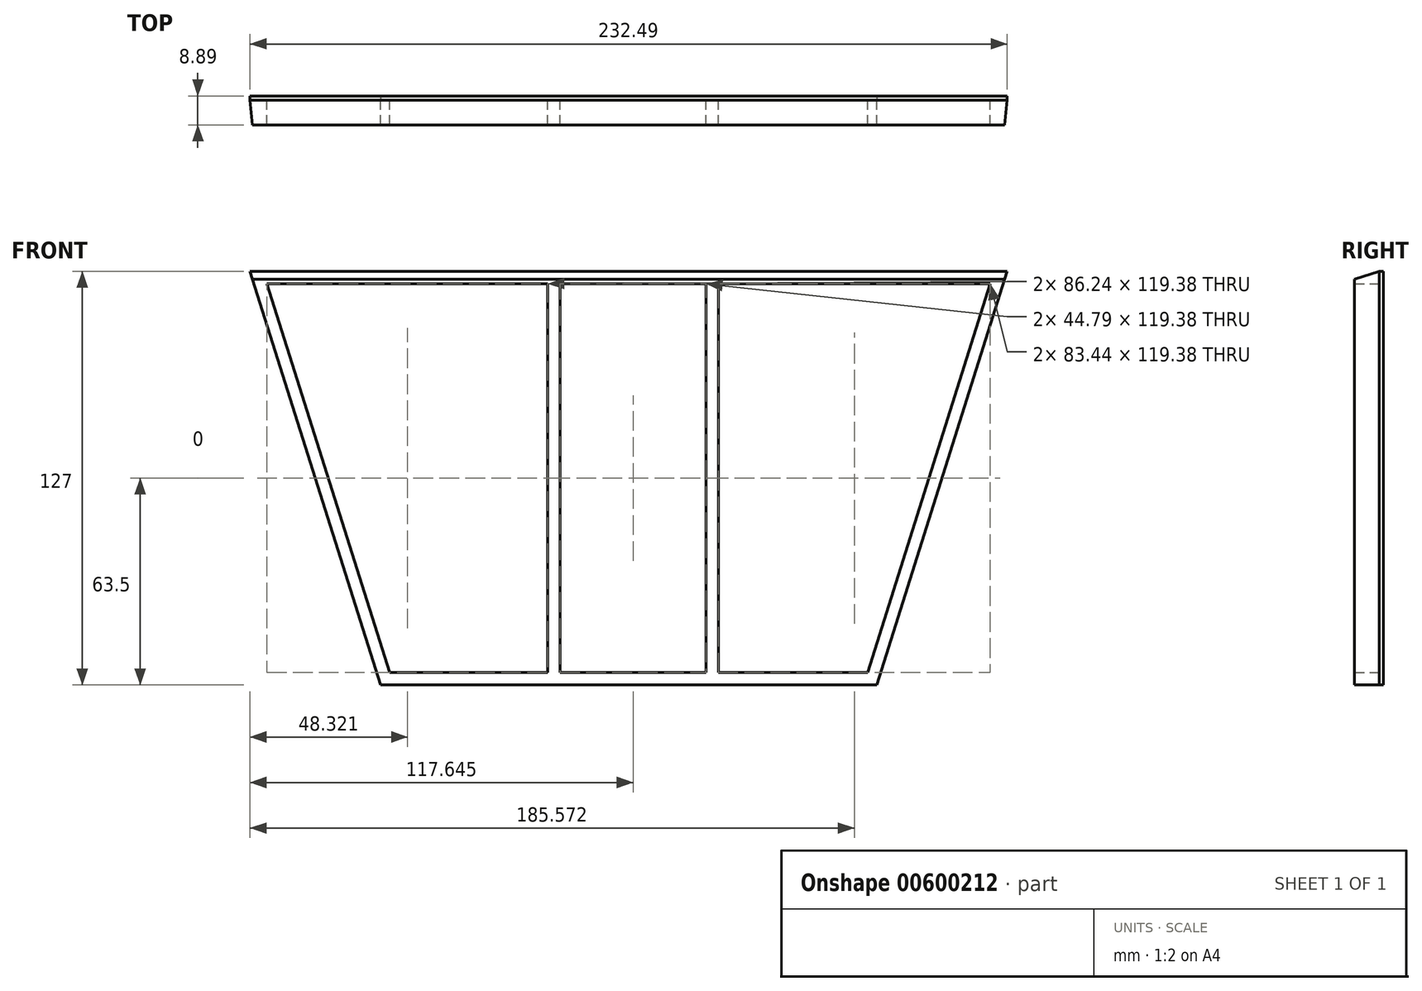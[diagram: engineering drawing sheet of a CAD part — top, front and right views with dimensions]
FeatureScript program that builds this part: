
annotation { "Feature Type Name" : "Feature", "Feature Type Description" : "" }
export const myFeature = defineFeature(function(context is Context, id is Id, definition is map)
    precondition{}
    {
        {
            var Q0;
            Q0=qCreatedBy(makeId("Front.planeOp"),FACE);
            var sketch = newSketch(context, id + "F0", { "sketchPlane" : qUnion([Q0])});
            skLineSegment(sketch, "E0", {"start": v(0, 0) * mm, "end": v(-232.49, 0) * mm});
            skLineSegment(sketch, "E1", {"start": v(-232.49, 0) * mm, "end": v(-192.44, -127) * mm});
            skLineSegment(sketch, "E2", {"start": v(-192.44, -127) * mm, "end": v(-40.04, -127) * mm});
            skLineSegment(sketch, "E3", {"start": v(-40.04, -127) * mm, "end": v(0, 0) * mm});
            skLineSegment(sketch, "E4.0", {"start": v(-5.2, -3.8) * mm, "end": v(-227.29, -3.81) * mm});
            skLineSegment(sketch, "E4.1", {"start": v(-42.84, -123.2) * mm, "end": v(-5.2, -3.81) * mm});
            skLineSegment(sketch, "E4.2", {"start": v(-189.65, -123.2) * mm, "end": v(-42.84, -123.2) * mm});
            skLineSegment(sketch, "E4.3", {"start": v(-227.29, -3.81) * mm, "end": v(-189.65, -123.2) * mm});
            skLineSegment(sketch, "E5", {"start": v(-141.05, -3.81) * mm, "end": v(-141.05, -123.2) * mm});
            skLineSegment(sketch, "E6", {"start": v(-137.24, -3.81) * mm, "end": v(-137.24, -123.2) * mm});
            skLineSegment(sketch, "E7", {"start": v(-92.45, -3.81) * mm, "end": v(-92.45, -123.2) * mm});
            skLineSegment(sketch, "E8", {"start": v(-88.64, -3.81) * mm, "end": v(-88.64, -123.2) * mm});
            skLineSegment(sketch, "E9.bottom", {"start": v(-189.65, -123.2) * mm, "end": v(-185.84, -123.2) * mm});
            skLineSegment(sketch, "E9.top", {"start": v(-189.65, -3.81) * mm, "end": v(-185.84, -3.81) * mm});
            skLineSegment(sketch, "E9.left", {"start": v(-189.65, -123.2) * mm, "end": v(-189.65, -3.81) * mm});
            skLineSegment(sketch, "E9.right", {"start": v(-185.84, -123.2) * mm, "end": v(-185.84, -3.81) * mm});
            skLineSegment(sketch, "E10.bottom", {"start": v(-42.84, -123.2) * mm, "end": v(-46.65, -123.2) * mm});
            skLineSegment(sketch, "E10.top", {"start": v(-42.84, -3.8) * mm, "end": v(-46.65, -3.8) * mm});
            skLineSegment(sketch, "E10.left", {"start": v(-42.84, -123.2) * mm, "end": v(-42.84, -3.8) * mm});
            skLineSegment(sketch, "E10.right", {"start": v(-46.65, -123.2) * mm, "end": v(-46.65, -3.8) * mm});
            skSolve(sketch);
        }
        {
            var Q0;
            Q0=makeQuery(id+"F0.imprint","IMPRINT",FACE,{"disambiguationData":[TD([[makeQuery(id+"F0.imprint","IMPRINT",EDGE,{"derivedFrom":sQuery(id+"F0.wireOp",EDGE,"E0")}),1.0]])]});
            var Q1;
            {var subQ0=sQuery(id+"F0.wireOp",EDGE,"E5");Q1=makeQuery(id+"F0.imprint","IMPRINT",FACE,{"disambiguationData":[TD([[makeQuery(id+"F0.imprint","IMPRINT",EDGE,{"derivedFrom":subQ0}),1.0]])]});}
            var Q2;
            {var subQ0=sQuery(id+"F0.wireOp",EDGE,"E7");Q2=makeQuery(id+"F0.imprint","IMPRINT",FACE,{"disambiguationData":[TD([[makeQuery(id+"F0.imprint","IMPRINT",EDGE,{"derivedFrom":subQ0}),1.0]])]});}
            var Q3;
            Q3=makeQuery(id+"F0.imprint","IMPRINT",FACE,{"disambiguationData":[TD([[makeQuery(id+"F0.imprint","IMPRINT",EDGE,{"derivedFrom":sQuery(id+"F0.wireOp",EDGE,"E9.bottom")}),1.0]])]});
            var Q4;
            Q4=makeQuery(id+"F0.imprint","IMPRINT",FACE,{"disambiguationData":[TD([[makeQuery(id+"F0.imprint","IMPRINT",EDGE,{"derivedFrom":sQuery(id+"F0.wireOp",EDGE,"E10.bottom")}),-1.0]])]});
            extrude(context, id + "F1", {"entities" : qUnion([Q0, Q1, Q2, Q3, Q4]), "depth" : 7.62 * mm, "offsetDistance" : 25.4 * mm});
        }
        {
            var Q0;
            Q0=qCreatedBy(makeId("Right.planeOp"),FACE);
            var sketch = newSketch(context, id + "F2", { "sketchPlane" : qUnion([Q0])});
            skLineSegment(sketch, "E11", {"start": v(0, 0) * mm, "end": v(-12.7, -4) * mm});
            skLineSegment(sketch, "E12", {"start": v(-12.7, -4) * mm, "end": v(-12.7, 0) * mm});
            skLineSegment(sketch, "E13", {"start": v(-12.7, 0) * mm, "end": v(0, 0) * mm});
            skSolve(sketch);
        }
        {
            var Q0;
            Q0=makeQuery(id+"F2.imprint","IMPRINT",FACE,{"disambiguationData":[TD([[makeQuery(id+"F2.imprint","IMPRINT",EDGE,{"derivedFrom":sQuery(id+"F2.wireOp",EDGE,"E11")}),-1.0]])]});
            extrude(context, id + "F3", {"entities" : qUnion([Q0]), "operationType" : NewBodyOperationType.REMOVE, "oppositeDirection" : true, "depth" : 2159 * mm, "offsetDistance" : 25.4 * mm});
        }
        {
            var Q0;
            Q0=qCreatedBy(makeId("Front.planeOp"),FACE);
            var sketch = newSketch(context, id + "F4", { "sketchPlane" : qUnion([Q0])});
            skLineSegment(sketch, "E14", {"start": v(0, 0) * mm, "end": v(-232.49, 0) * mm});
            skLineSegment(sketch, "E15", {"start": v(-232.49, 0) * mm, "end": v(-192.44, -127) * mm});
            skLineSegment(sketch, "E16", {"start": v(-192.44, -127) * mm, "end": v(-40.04, -127) * mm});
            skLineSegment(sketch, "E17", {"start": v(-40.04, -127) * mm, "end": v(0, 0) * mm});
            skSolve(sketch);
        }
        {
            var Q0;
            Q0=makeQuery(id+"F4.imprint","IMPRINT",FACE,{"disambiguationData":[TD([[makeQuery(id+"F4.imprint","IMPRINT",EDGE,{"derivedFrom":sQuery(id+"F4.wireOp",EDGE,"E14")}),1.0]])]});
            extrude(context, id + "F5", {"entities" : qUnion([Q0]), "oppositeDirection" : true, "depth" : 1.27 * mm, "offsetDistance" : 25.4 * mm});
        }
    });
